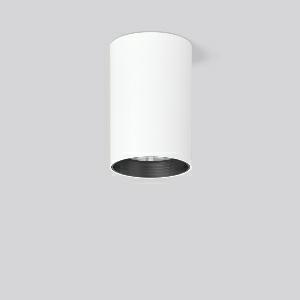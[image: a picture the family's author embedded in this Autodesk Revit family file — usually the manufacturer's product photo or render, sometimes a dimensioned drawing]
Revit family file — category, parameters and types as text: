
# Revit family: heledon_maxi_a_931234_002_76_4385
name_source: partatom
category: Lighting Fixtures
units: mm (PartAtom-declared; Revit-internal decimal feet)

## family parameters
Cut with Voids When Loaded = No
Host = Face
Light Source = No
Part Type = Normal
Room Calculation Point = No
Round Connector Dimension = Use Diameter
Shared = No

## types (1)
- HELEDON maxi A (1 x LED Modul 932 fresh meat, 1800 lm, 3200)
    Apparent Load = 33 VA
    Approval mark = CE
    CIE Flux Codes = 97 100 100 100 100
    Color Rendering = 90
    Color Temperature = 3200
    Default Elevation = 1800 mm  [stored 5.90551 ft]
    Description = Series: HELEDON maxi
Cylindrical surface-mounted downlight. Housing: die-cast aluminium, powder-coated. Internal ceiling frame polycarbonate with bayonet mounting. Black plastic ring and recessed LED to prevent glare from the side. Optical assembly with lens made of plastic (polycarbonate) for the best homogeneous light distribution - can be changed without tools. Special LED for illumination of meat included. Suitable for Ceiling mounting. Easy installation with a separate ceiling frame with bayonet mounting and plug connection. Driver integrated. Connected via plug-in connector. High quality converter without flickering and stroboscopic effect. The following accessories can be mounted without use of tools: interchangeable lenses, decorative glasses, honeycomb louvre, clear and frosted diffusers, white interchangeable plastic ring. 
Colour: traffic white, matt (RAL 9016)
Diameter: 123 mm
Height: 183 mm
Lamp: LED
Socket: without socket
Colour temperature: fresh meat
System power: 33 W
Rated luminous flux: 1800 lm
Luminous efficiency: 55 lm/W
Control gear: Converter, dimmable, DALI
Protection class: I
Type of protection: IP 20
    Height = 183 mm
    Lamp = 1 x LED Modul 932 fresh meat
    Lamp Light Flux = 1800 lm
    Lamp count = 1
    Length = 123 mm
    Lifetime = 50000 h
    Luminous efficacy = 55 lm/W
    Manufacturer = RZB
    ModVariant = No
    Model = 931234.002.76
    Mounting Place = Ceiling
    Mounting Type = Surface mounted
    Number of Poles = 1
    OnlyDefault = Yes
    Power Factor = 1
    Product Name = HELEDON maxi A
    Product group = Surface mounted downlights
    ProductGroupID = 302
    Protection Class = Protection class I
    Protection Degree = IP 20
    RLX_Detail_Level = 1
    RLX_Emergency_Light_Flux = 0 lm
    RLX_Emergency_Type = 0
    RLX_Emergency_Type_DB = No
    RlxData = <blob elided: 97973 chars, md5=c67c344d>
    Socket = socket
    Standby Power = 0 W
    System Light Flux = 1800 lm
    System Power = 33 W
    Type Comments = Product without accessories
    Type Image = 931193.002.jpg
    URL = http://relux.com
    VarID = ---
    Voltage = 230 V
    Voltage Range = 220-240 V
    Weight = 0.00 kg
    Width = 0 mm  [stored 0 ft]

note: [stored X ft] marks values corroborated as IEEE doubles in the binary element streams (Revit-internal decimal feet)

## geometry (parser evidence)
native form markers: Blend x4, Sweep x10
no freeform markers — native parametric forms only
